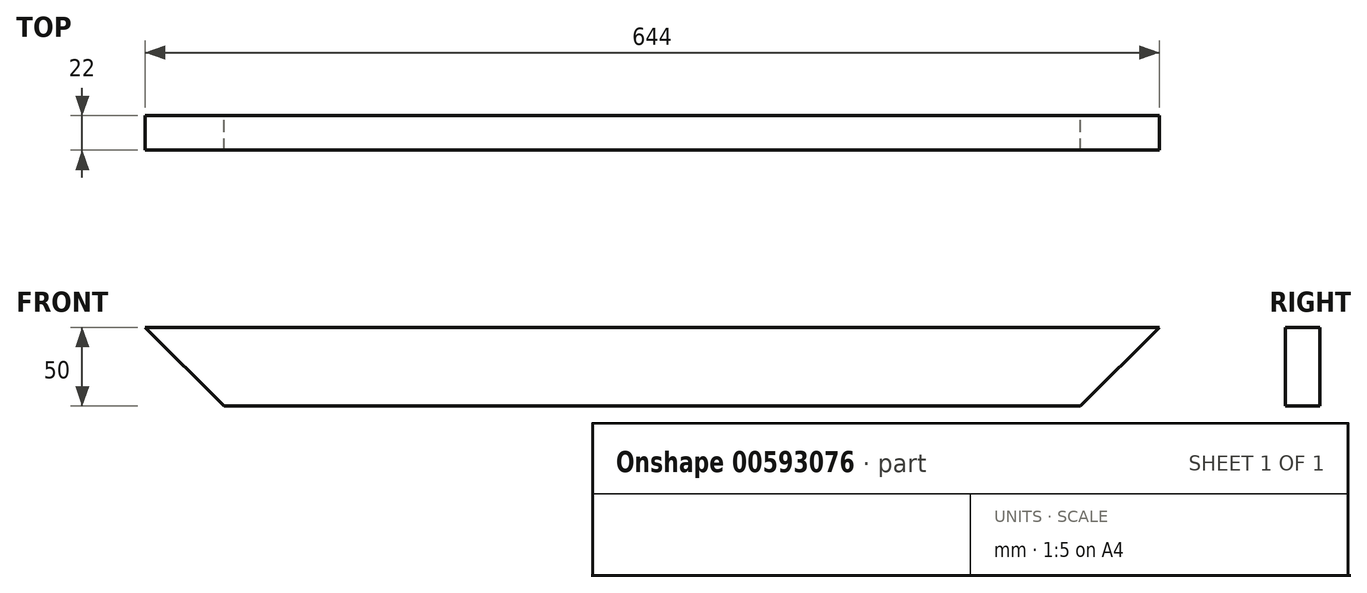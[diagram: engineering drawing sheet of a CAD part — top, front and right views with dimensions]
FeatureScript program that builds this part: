
annotation { "Feature Type Name" : "Feature", "Feature Type Description" : "" }
export const myFeature = defineFeature(function(context is Context, id is Id, definition is map)
    precondition{}
    {
        {
            var Q0;
            Q0=qCreatedBy(makeId("Front.planeOp"),FACE);
            var sketch = newSketch(context, id + "F0", { "sketchPlane" : qUnion([Q0])});
            skLineSegment(sketch, "E0.bottom", {"start": v(-322, 0) * mm, "end": v(322, 0) * mm});
            skLineSegment(sketch, "E0.top", {"start": v(-272, -50) * mm, "end": v(272, -50) * mm});
            skLineSegment(sketch, "E1", {"start": v(-322, 0) * mm, "end": v(-272, -50) * mm});
            skLineSegment(sketch, "E2", {"start": v(322, 0) * mm, "end": v(272, -50) * mm});
            skSolve(sketch);
        }
        {
            var Q0;
            Q0 = qSketchRegion(id + "F0", true);
            extrude(context, id + "F1", {"entities" : qUnion([Q0]), "depth" : 22 * mm, "offsetDistance" : 25 * mm});
        }
    });
